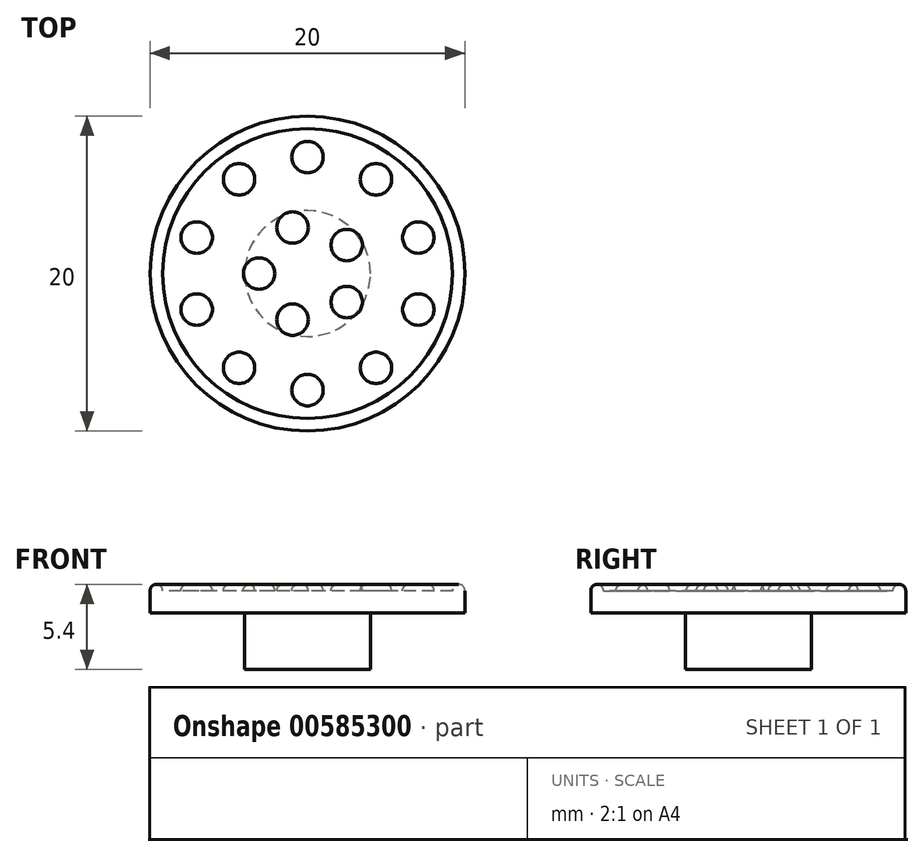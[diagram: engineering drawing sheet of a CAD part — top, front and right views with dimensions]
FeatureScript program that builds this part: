
annotation { "Feature Type Name" : "Feature", "Feature Type Description" : "" }
export const myFeature = defineFeature(function(context is Context, id is Id, definition is map)
    precondition{}
    {
        {
            var Q0;
            Q0=qCreatedBy(makeId("Top.planeOp"),FACE);
            var sketch = newSketch(context, id + "F0", { "sketchPlane" : qUnion([Q0])});
            skCircle(sketch, "E0", {"center": v(-37.5, 22.4) * mm, "radius": 10 * mm});
            skCircle(sketch, "E1", {"center": v(-37.5, 22.4) * mm, "radius": 4 * mm});
            skSolve(sketch);
        }
        {
            var Q0;
            Q0=makeQuery(id+"F0.imprint","IMPRINT",FACE,{"disambiguationData":[TD([[makeQuery(id+"F0.imprint","IMPRINT",EDGE,{"derivedFrom":sQuery(id+"F0.wireOp",EDGE,"E0")}),1.0]])]});
            var Q1;
            Q1=makeQuery(id+"F0.imprint","IMPRINT",FACE,{"disambiguationData":[TD([[makeQuery(id+"F0.imprint","IMPRINT",EDGE,{"derivedFrom":sQuery(id+"F0.wireOp",EDGE,"E1")}),1.0]])]});
            extrude(context, id + "F1", {"entities" : qUnion([Q0, Q1]), "oppositeDirection" : true, "depth" : 1.4 * mm, "offsetDistance" : 25 * mm});
        }
        {
            var Q0;
            Q0=makeQuery(id+"F0.imprint","IMPRINT",FACE,{"disambiguationData":[TD([[makeQuery(id+"F0.imprint","IMPRINT",EDGE,{"derivedFrom":sQuery(id+"F0.wireOp",EDGE,"E1")}),1.0]])]});
            extrude(context, id + "F2", {"entities" : qUnion([Q0]), "operationType" : NewBodyOperationType.ADD, "oppositeDirection" : true, "depth" : 5 * mm, "offsetDistance" : 25 * mm});
        }
        {
            var Q0;
            Q0=makeQuery(id+"F1.opExtrude","CAP_FACE",FACE,{"disambiguationData":[OSD([sQuery(id+"F0.wireOp",EDGE,"E0")])],"isStart":true});
            var sketch = newSketch(context, id + "F3", { "sketchPlane" : qUnion([Q0])});
            skCircle(sketch, "E2.0", {"center": v(-37.5, 22.4) * mm, "radius": 10 * mm});
            skCircle(sketch, "E3", {"center": v(-37.5, 22.4) * mm, "radius": 9.2 * mm});
            skCircle(sketch, "E4", {"center": v(-37.5, 29.8) * mm, "radius": 1 * mm});
            skCircle(sketch, "E5.1.0", {"center": v(-41.86, 28.38) * mm, "radius": 1 * mm});
            skCircle(sketch, "E5.2.0", {"center": v(-44.54, 24.68) * mm, "radius": 1 * mm});
            skCircle(sketch, "E6.1.3.0", {"center": v(-44.54, 20.1) * mm, "radius": 1 * mm});
            skCircle(sketch, "E6.1.4.0", {"center": v(-41.86, 16.4) * mm, "radius": 1 * mm});
            skCircle(sketch, "E6.1.5.0", {"center": v(-37.5, 15) * mm, "radius": 1 * mm});
            skCircle(sketch, "E6.1.6.0", {"center": v(-33.16, 16.4) * mm, "radius": 1 * mm});
            skCircle(sketch, "E6.1.7.0", {"center": v(-30.47, 20.1) * mm, "radius": 1 * mm});
            skCircle(sketch, "E6.1.8.0", {"center": v(-30.47, 24.68) * mm, "radius": 1 * mm});
            skCircle(sketch, "E6.1.9.0", {"center": v(-33.16, 28.38) * mm, "radius": 1 * mm});
            skCircle(sketch, "E7", {"center": v(-38.46, 25.32) * mm, "radius": 1 * mm});
            skCircle(sketch, "E8.1.0", {"center": v(-40.58, 22.4) * mm, "radius": 1 * mm});
            skCircle(sketch, "E8.2.0", {"center": v(-38.46, 19.47) * mm, "radius": 1 * mm});
            skCircle(sketch, "E8.3.0", {"center": v(-35.02, 20.59) * mm, "radius": 1 * mm});
            skCircle(sketch, "E8.4.0", {"center": v(-35.02, 24.2) * mm, "radius": 1 * mm});
            skLineSegment(sketch, "E9", {"start": v(-33.16, 28.38) * mm, "end": v(-35.02, 24.2) * mm, "construction": true});
            skLineSegment(sketch, "E10", {"start": v(-30.47, 24.68) * mm, "end": v(-35.02, 24.2) * mm, "construction": true});
            skLineSegment(sketch, "E11", {"start": v(-33.16, 28.38) * mm, "end": v(-30.47, 24.68) * mm, "construction": true});
            skCircle(sketch, "E12", {"center": v(-37.5, 22.4) * mm, "radius": 8.4 * mm});
            skSolve(sketch);
        }
        {
            var Q0;
            Q0=makeQuery(id+"F3.imprint","IMPRINT",FACE,{"disambiguationData":[TD([[makeQuery(id+"F3.imprint","IMPRINT",EDGE,{"derivedFrom":sQuery(id+"F3.wireOp",EDGE,"E2.0")}),1.0]])]});
            var Q1;
            Q1=makeQuery(id+"F3.imprint","IMPRINT",FACE,{"disambiguationData":[TD([[makeQuery(id+"F3.imprint","IMPRINT",EDGE,{"derivedFrom":sQuery(id+"F3.wireOp",EDGE,"E5.2.0")}),1.0]])]});
            var Q2;
            Q2=makeQuery(id+"F3.imprint","IMPRINT",FACE,{"disambiguationData":[TD([[makeQuery(id+"F3.imprint","IMPRINT",EDGE,{"derivedFrom":sQuery(id+"F3.wireOp",EDGE,"E6.1.3.0")}),1.0]])]});
            var Q3;
            Q3=makeQuery(id+"F3.imprint","IMPRINT",FACE,{"disambiguationData":[TD([[makeQuery(id+"F3.imprint","IMPRINT",EDGE,{"derivedFrom":sQuery(id+"F3.wireOp",EDGE,"E6.1.4.0")}),1.0]])]});
            var Q4;
            Q4=makeQuery(id+"F3.imprint","IMPRINT",FACE,{"disambiguationData":[TD([[makeQuery(id+"F3.imprint","IMPRINT",EDGE,{"derivedFrom":sQuery(id+"F3.wireOp",EDGE,"E4")}),1.0]])]});
            var Q5;
            Q5=makeQuery(id+"F3.imprint","IMPRINT",FACE,{"disambiguationData":[TD([[makeQuery(id+"F3.imprint","IMPRINT",EDGE,{"derivedFrom":sQuery(id+"F3.wireOp",EDGE,"E5.1.0")}),1.0]])]});
            var Q6;
            Q6=makeQuery(id+"F3.imprint","IMPRINT",FACE,{"disambiguationData":[TD([[makeQuery(id+"F3.imprint","IMPRINT",EDGE,{"derivedFrom":sQuery(id+"F3.wireOp",EDGE,"E6.1.5.0")}),1.0]])]});
            var Q7;
            Q7=makeQuery(id+"F3.imprint","IMPRINT",FACE,{"disambiguationData":[TD([[makeQuery(id+"F3.imprint","IMPRINT",EDGE,{"derivedFrom":sQuery(id+"F3.wireOp",EDGE,"E6.1.6.0")}),1.0]])]});
            var Q8;
            Q8=makeQuery(id+"F3.imprint","IMPRINT",FACE,{"disambiguationData":[TD([[makeQuery(id+"F3.imprint","IMPRINT",EDGE,{"derivedFrom":sQuery(id+"F3.wireOp",EDGE,"E6.1.7.0")}),1.0]])]});
            var Q9;
            Q9=makeQuery(id+"F3.imprint","IMPRINT",FACE,{"disambiguationData":[TD([[makeQuery(id+"F3.imprint","IMPRINT",EDGE,{"derivedFrom":sQuery(id+"F3.wireOp",EDGE,"E6.1.8.0")}),1.0]])]});
            var Q10;
            Q10=makeQuery(id+"F3.imprint","IMPRINT",FACE,{"disambiguationData":[TD([[makeQuery(id+"F3.imprint","IMPRINT",EDGE,{"derivedFrom":sQuery(id+"F3.wireOp",EDGE,"E6.1.9.0")}),1.0]])]});
            var Q11;
            Q11=makeQuery(id+"F3.imprint","IMPRINT",FACE,{"disambiguationData":[TD([[makeQuery(id+"F3.imprint","IMPRINT",EDGE,{"derivedFrom":sQuery(id+"F3.wireOp",EDGE,"E7")}),1.0]])]});
            var Q12;
            Q12=makeQuery(id+"F3.imprint","IMPRINT",FACE,{"disambiguationData":[TD([[makeQuery(id+"F3.imprint","IMPRINT",EDGE,{"derivedFrom":sQuery(id+"F3.wireOp",EDGE,"E8.1.0")}),1.0]])]});
            var Q13;
            Q13=makeQuery(id+"F3.imprint","IMPRINT",FACE,{"disambiguationData":[TD([[makeQuery(id+"F3.imprint","IMPRINT",EDGE,{"derivedFrom":sQuery(id+"F3.wireOp",EDGE,"E8.2.0")}),1.0]])]});
            var Q14;
            Q14=makeQuery(id+"F3.imprint","IMPRINT",FACE,{"disambiguationData":[TD([[makeQuery(id+"F3.imprint","IMPRINT",EDGE,{"derivedFrom":sQuery(id+"F3.wireOp",EDGE,"E8.3.0")}),1.0]])]});
            var Q15;
            Q15=makeQuery(id+"F3.imprint","IMPRINT",FACE,{"disambiguationData":[TD([[makeQuery(id+"F3.imprint","IMPRINT",EDGE,{"derivedFrom":sQuery(id+"F3.wireOp",EDGE,"E8.4.0")}),1.0]])]});
            extrude(context, id + "F4", {"entities" : qUnion([Q0, Q1, Q2, Q3, Q4, Q5, Q6, Q7, Q8, Q9, Q10, Q11, Q12, Q13, Q14, Q15]), "operationType" : NewBodyOperationType.ADD, "depth" : .4 * mm, "offsetDistance" : 25 * mm});
        }
        {
            var Q0;
            Q0=makeQuery(id+"F4.opExtrude","CAP_EDGE",EDGE,{"disambiguationData":[OSD([sQuery(id+"F3.wireOp",EDGE,"E5.2.0")])],"isStart":false});
            var Q1;
            Q1=makeQuery(id+"F4.opExtrude","CAP_EDGE",EDGE,{"disambiguationData":[OSD([sQuery(id+"F3.wireOp",EDGE,"E6.1.3.0")])],"isStart":false});
            var Q2;
            Q2=makeQuery(id+"F4.opExtrude","CAP_EDGE",EDGE,{"disambiguationData":[OSD([sQuery(id+"F3.wireOp",EDGE,"E6.1.4.0")])],"isStart":false});
            var Q3;
            Q3=makeQuery(id+"F4.opExtrude","CAP_EDGE",EDGE,{"disambiguationData":[OSD([sQuery(id+"F3.wireOp",EDGE,"E8.2.0")])],"isStart":false});
            var Q4;
            Q4=makeQuery(id+"F4.opExtrude","CAP_EDGE",EDGE,{"disambiguationData":[OSD([sQuery(id+"F3.wireOp",EDGE,"E8.1.0")])],"isStart":false});
            var Q5;
            Q5=makeQuery(id+"F4.opExtrude","CAP_EDGE",EDGE,{"disambiguationData":[OSD([sQuery(id+"F3.wireOp",EDGE,"E8.3.0")])],"isStart":false});
            var Q6;
            Q6=makeQuery(id+"F4.opExtrude","CAP_EDGE",EDGE,{"disambiguationData":[OSD([sQuery(id+"F3.wireOp",EDGE,"E6.1.5.0")])],"isStart":false});
            var Q7;
            Q7=makeQuery(id+"F4.opExtrude","CAP_EDGE",EDGE,{"disambiguationData":[OSD([sQuery(id+"F3.wireOp",EDGE,"E6.1.6.0")])],"isStart":false});
            var Q8;
            Q8=makeQuery(id+"F4.opExtrude","CAP_EDGE",EDGE,{"disambiguationData":[OSD([sQuery(id+"F3.wireOp",EDGE,"E6.1.7.0")])],"isStart":false});
            var Q9;
            Q9=makeQuery(id+"F4.opExtrude","CAP_EDGE",EDGE,{"disambiguationData":[OSD([sQuery(id+"F3.wireOp",EDGE,"E6.1.8.0")])],"isStart":false});
            var Q10;
            Q10=makeQuery(id+"F4.opExtrude","CAP_EDGE",EDGE,{"disambiguationData":[OSD([sQuery(id+"F3.wireOp",EDGE,"E8.4.0")])],"isStart":false});
            var Q11;
            Q11=makeQuery(id+"F4.opExtrude","CAP_EDGE",EDGE,{"disambiguationData":[OSD([sQuery(id+"F3.wireOp",EDGE,"E7")])],"isStart":false});
            var Q12;
            Q12=makeQuery(id+"F4.opExtrude","CAP_EDGE",EDGE,{"disambiguationData":[OSD([sQuery(id+"F3.wireOp",EDGE,"E5.1.0")])],"isStart":false});
            var Q13;
            Q13=makeQuery(id+"F4.opExtrude","CAP_EDGE",EDGE,{"disambiguationData":[OSD([sQuery(id+"F3.wireOp",EDGE,"E4")])],"isStart":false});
            var Q14;
            Q14=makeQuery(id+"F4.opExtrude","CAP_EDGE",EDGE,{"disambiguationData":[OSD([sQuery(id+"F3.wireOp",EDGE,"E6.1.9.0")])],"isStart":false});
            var Q15;
            Q15=makeQuery(id+"F4.opExtrude","CAP_EDGE",EDGE,{"disambiguationData":[OSD([sQuery(id+"F3.wireOp",EDGE,"E3")])],"isStart":false});
            var Q16;
            Q16=makeQuery(id+"F4.opExtrude","CAP_EDGE",EDGE,{"disambiguationData":[OSD([sQuery(id+"F3.wireOp",EDGE,"E2.0")])],"isStart":false});
            fillet(context, id + "F5", {"entities" : qUnion([Q0, Q1, Q2, Q3, Q4, Q5, Q6, Q7, Q8, Q9, Q10, Q11, Q12, Q13, Q14, Q15, Q16]), "radius" : .4 * mm, "tangentPropagation" : true, "allowEdgeOverflow" : false});
        }
    });
